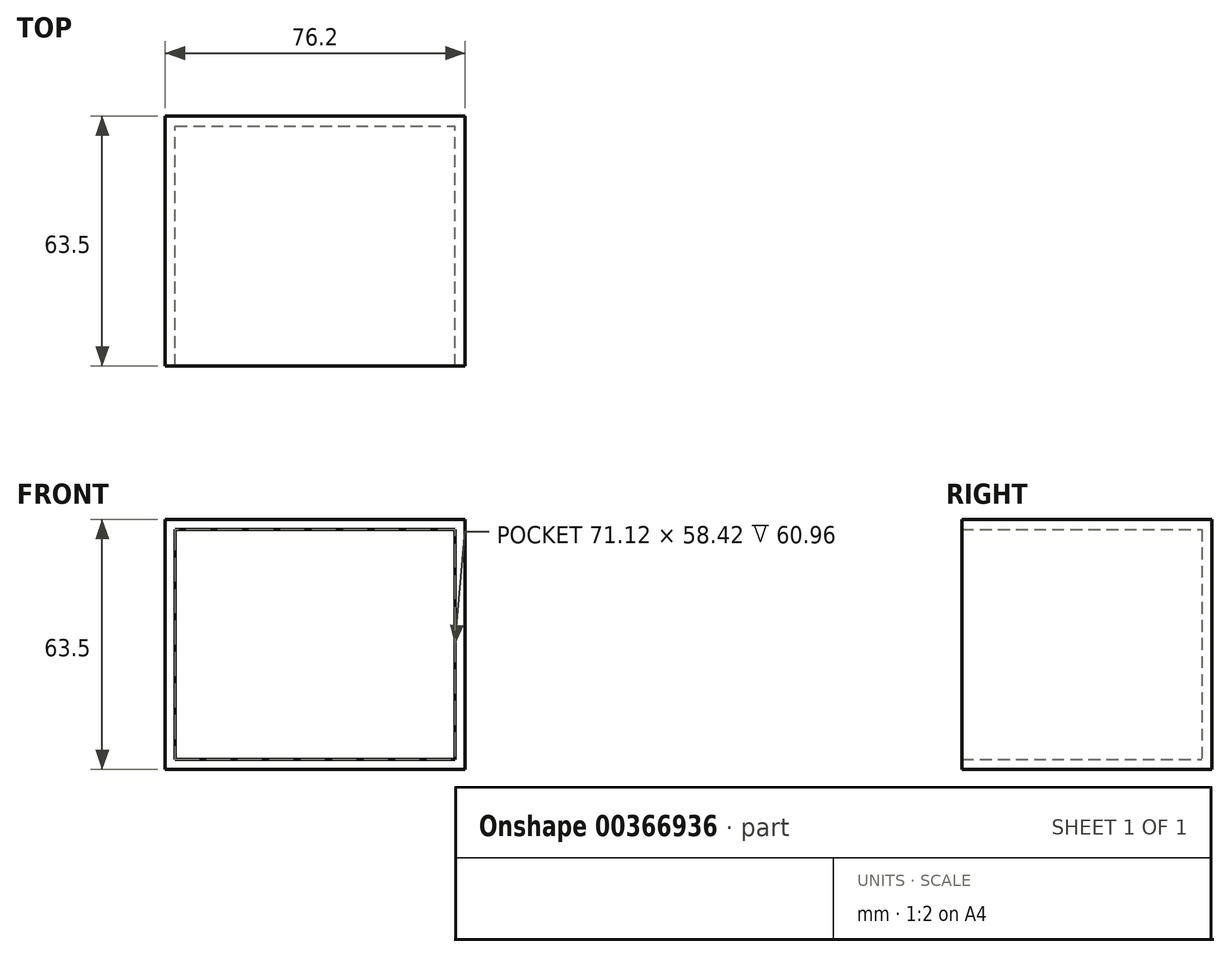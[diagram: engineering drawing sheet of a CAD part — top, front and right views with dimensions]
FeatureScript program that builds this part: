
annotation { "Feature Type Name" : "Feature", "Feature Type Description" : "" }
export const myFeature = defineFeature(function(context is Context, id is Id, definition is map)
    precondition{}
    {
        {
            var Q0;
            Q0=qCreatedBy(makeId("Front.planeOp"),FACE);
            var sketch = newSketch(context, id + "F0", { "sketchPlane" : qUnion([Q0])});
            skLineSegment(sketch, "E0.bottom", {"start": v(0, 0) * mm, "end": v(12.7, 0) * mm});
            skLineSegment(sketch, "E0.top", {"start": v(0, -63.5) * mm, "end": v(12.7, -63.5) * mm});
            skLineSegment(sketch, "E0.left", {"start": v(0, 0) * mm, "end": v(0, -63.5) * mm});
            skLineSegment(sketch, "E0.right", {"start": v(12.7, 0) * mm, "end": v(12.7, -63.5) * mm});
            skSolve(sketch);
        }
        {
            var Q0;
            Q0=makeQuery(id+"F0.imprint","IMPRINT",FACE,{"disambiguationData":[TD([[makeQuery(id+"F0.imprint","IMPRINT",EDGE,{"derivedFrom":sQuery(id+"F0.wireOp",EDGE,"E0.bottom")}),-1.0]])]});
            extrude(context, id + "F1", {"entities" : qUnion([Q0]), "depth" : 63.5 * mm});
        }
        {
            var Q0;
            Q0=makeQuery(id+"F1.opExtrude","SWEPT_FACE",FACE,{"disambiguationData":[OSD([sQuery(id+"F0.wireOp",EDGE,"E0.right")])]});
            var sketch = newSketch(context, id + "F2", { "sketchPlane" : qUnion([Q0])});
            skSolve(sketch);
        }
        {
            var Q0;
            {var subQ0=sQuery(id+"F0.wireOp",EDGE,"E0.right");Q0=makeQuery(id+"F2.imprint","IMPRINT",FACE,{"disambiguationData":[TD([[makeQuery(id+"F2.imprint","IMPRINT",EDGE,{"derivedFrom":makeQuery(id+"F1.opExtrude","CAP_EDGE",EDGE,{"disambiguationData":[OSD([subQ0])],"isStart":true})}),-1.0]])]});}
            extrude(context, id + "F3", {"entities" : qUnion([Q0]), "operationType" : NewBodyOperationType.ADD, "depth" : 63.5 * mm});
        }
        {
            var Q0;
            {var subQ0=sQuery(id+"F0.wireOp",EDGE,"E0.right");Q0=makeQuery(id+"F3.boolean.opBoolean","MERGE",FACE,{"derivedFrom":[makeQuery(id+"F1.opExtrude","CAP_FACE",FACE,{"disambiguationData":[OSD([sQuery(id+"F0.wireOp",EDGE,"E0.bottom"),sQuery(id+"F0.wireOp",EDGE,"E0.top"),sQuery(id+"F0.wireOp",EDGE,"E0.left"),subQ0])],"isStart":false}),makeQuery(id+"F3.opExtrude","SWEPT_FACE",FACE,{"disambiguationData":[OSD([subQ0]),TDD([makeQuery(id+"F2.imprint","IMPRINT",EDGE,{"derivedFrom":makeQuery(id+"F1.opExtrude","CAP_EDGE",EDGE,{"disambiguationData":[OSD([subQ0])],"isStart":false})})])]})]});}
            shell(context, id + "F4", {"entities" : qUnion([Q0]), "thickness" : 2.54 * mm});
        }
    });
